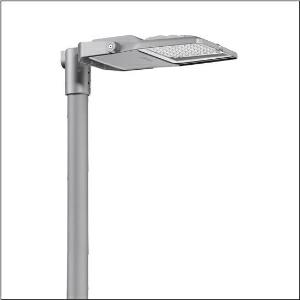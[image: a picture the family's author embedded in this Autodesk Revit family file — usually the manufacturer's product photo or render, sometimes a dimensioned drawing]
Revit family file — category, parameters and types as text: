
# Revit family: floodlight_fl_21_iq_mini___pl33t_5xa7772b4f3a_8cfb
name_source: partatom
category: Lighting Fixtures
units: mm (PartAtom-declared; Revit-internal decimal feet)

## family parameters
Cut with Voids When Loaded = No
Host = Face
Light Source = No
Part Type = Normal
Room Calculation Point = No
Round Connector Dimension = Use Diameter
Shared = No

## types (1)
- --- (1 x LED, 6420 lm, 45.5 W, 4000K)
    Apparent Load = 46 VA
    CIE Flux Codes = 26 75 99 100 100
    Color Rendering = 70
    Color Temperature = 4000K
    Default Elevation = 1800 mm
    Description = Floodlight FL 21 iQ mini, floodlight, primary light control with lens, of PMMA, primary optical cover: protective disc, of toughened safety glass, transparent, light distribution: PL33T, light emission: direct distribution, installation type: surface-mounted, LED, High Power LED, rated luminous flux: 6.420lm, luminous efficacy: 141lm/W, light colour: 740, colour temperature: 4000K, control: Auto-Match, Temp-Guard, Night-Set, Smart-Wire, Desk-Remote (wireless, voltage-free reading and setting of iQ features in the workshop via application-optimized NFC function/RFID function), optimised constant luminous flux control (CLO 2.0), Light-Fading, Lumen-Switch, with terminal, 6-pole, mains connection: 220..240V, AC, 50/60Hz, start of lifetime: 46W, end of service life: 48W, reduction: 22W, luminaire housing, of diecast aluminium, powder-coated, Siteco® metallic grey (DB 702S), corrosivity category C5 mid according to DIN EN ISO 12944, sealing non-destructively replaceable, please order mast flange separately, mast bracket, of steel, galvanised, powder-coated, protection rating (complete): IP66, insulation class (complete): insulation class II (safety insulation), certification: CE, ENEC, VDE, protection symbol: D, impact resistance: IK08, permissible operating ambient temperature: -40..+40°C, permissible operating ambient temperature for outdoor applications: -40..+50°C, standard: DIN EN 12944, LABS conformity tested according to VDMA 24364:2018-05, packaging unit: 1 piece

Light Distribution: PL33T
    Height = 70 mm
    Lamp = 1 x LED
    Lamp Light Flux = 6420 lm
    Lamp Power = 45.5 W
    Lamp count = 1
    Length = 485 mm
    Luminous efficacy = 141 lm/W
    Manufacturer = Siteco
    ModVariant = No
    Model = 5XA7772B4F3A
    Number of Poles = 1
    OnlyDefault = Yes
    Power Factor = 1
    Product Name = Floodlight FL 21 iQ mini | PL33T
    Product group = floodlight | pylon annexe
    ProductGroupID = 6200
    Protection Class = Protection class II
    Protection Degree = IP 66
    RLX_Detail_Level = 1
    RLX_Emergency_Light_Flux = 0 lm
    RLX_Emergency_Type = 0
    RLX_Emergency_Type_DB = No
    RlxData = <blob elided: 101065 chars, md5=b2069f6d>
    Socket = socket
    Standby Power = 0 W
    System Light Flux = 6420 lm
    System Power = 46 W
    Type Comments = factory setting: luminous flux: 100 % | dim-lin: 254 | 463 mA
    Type Image = l_1007125.jpg
    URL = http://relux.com
    VarID = @adj_082371
    Voltage = 0 V
    Weight = 0.00 kg
    Width = 337 mm

## geometry (parser evidence)
native form markers: Blend x4, Sweep x13
no freeform markers — native parametric forms only
